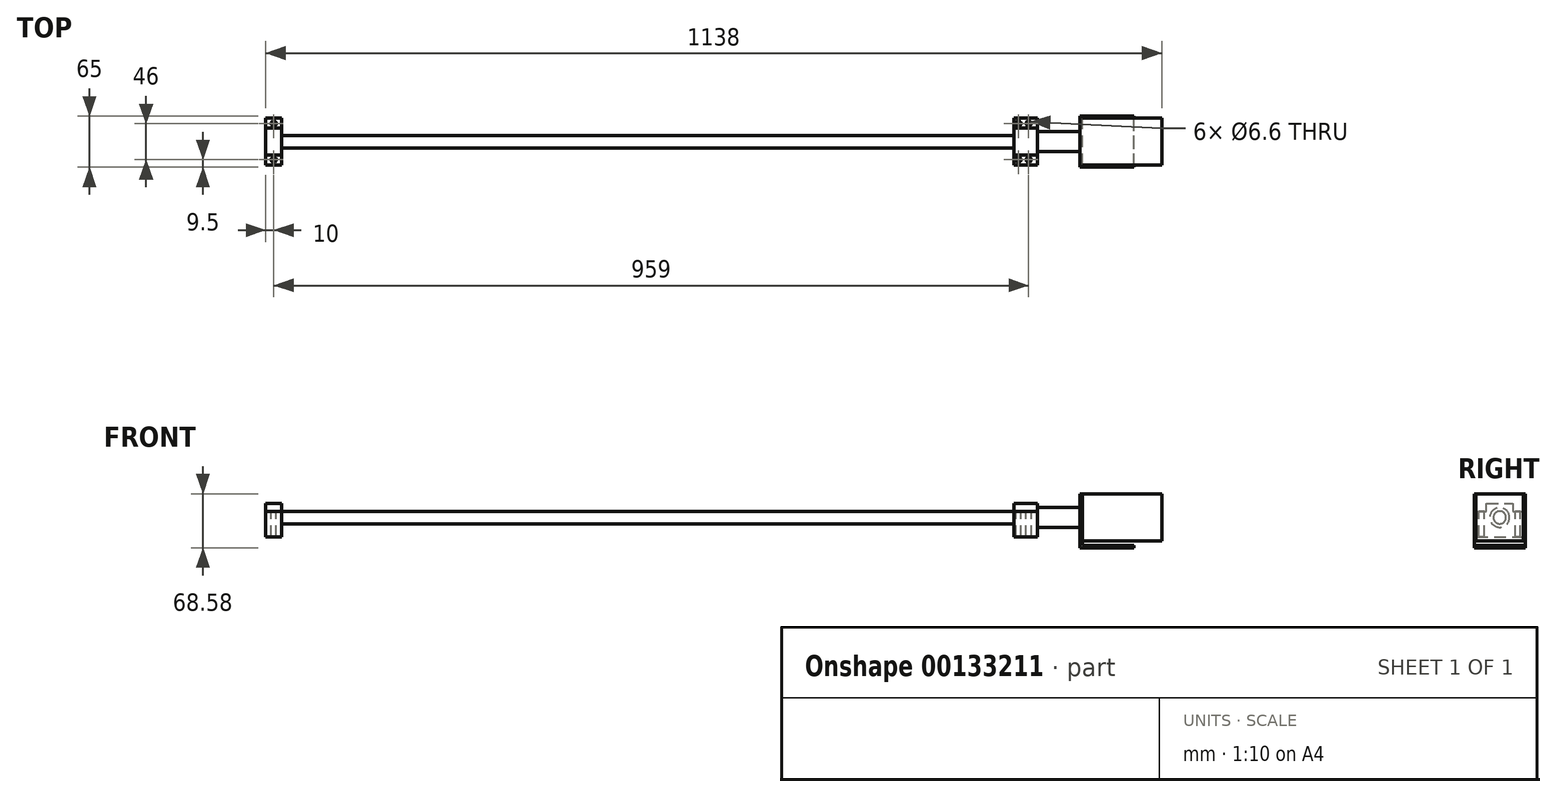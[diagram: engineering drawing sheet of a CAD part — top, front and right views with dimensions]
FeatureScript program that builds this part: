
annotation { "Feature Type Name" : "Feature", "Feature Type Description" : "" }
export const myFeature = defineFeature(function(context is Context, id is Id, definition is map)
    precondition{}
    {
        {
            var Q0;
            Q0=qCreatedBy(makeId("Right.planeOp"),FACE);
            var sketch = newSketch(context, id + "F0", { "sketchPlane" : qUnion([Q0])});
            skCircle(sketch, "E0", {"center": v(0, 0) * mm, "radius": 8 * mm});
            skSolve(sketch);
        }
        {
            var Q0;
            Q0=qSketchRegion(id+"F0",true);
            var Q1;
            Q1 = qSketchRegion(id + "F2", true);
            extrude(context, id + "F1", {"entities" : qUnion([Q0, Q1]), "depth" : 980 * mm, "offsetDistance" : 25 * mm});
        }
        {
            var Q0;
            Q0=makeQuery(id+"F1.opExtrude","CAP_FACE",FACE,{"disambiguationData":[OSD([sQuery(id+"F0.wireOp",EDGE,"E0")])],"isStart":false});
            var sketch = newSketch(context, id + "F2", { "sketchPlane" : qUnion([Q0])});
            skLineSegment(sketch, "E1.bottom", {"start": v(17, 7.5) * mm, "end": v(30, 7.5) * mm});
            skLineSegment(sketch, "E1.top", {"start": v(-30, -25) * mm, "end": v(30, -25) * mm});
            skLineSegment(sketch, "E1.left", {"start": v(-30, 7.5) * mm, "end": v(-30, -25) * mm});
            skLineSegment(sketch, "E1.right", {"start": v(30, 7.5) * mm, "end": v(30, -25) * mm});
            skLineSegment(sketch, "E2", {"start": v(-17, 7.5) * mm, "end": v(-17, 18) * mm});
            skLineSegment(sketch, "E3", {"start": v(-17, 18) * mm, "end": v(17, 18) * mm});
            skLineSegment(sketch, "E4", {"start": v(17, 18) * mm, "end": v(17, 7.5) * mm});
            skLineSegment(sketch, "E5", {"start": v(-30, 7.5) * mm, "end": v(-17, 7.5) * mm});
            skSolve(sketch);
        }
        {
            var Q0;
            Q0=qSketchRegion(id+"F2",true);
            extrude(context, id + "F3", {"entities" : qUnion([Q0]), "operationType" : NewBodyOperationType.ADD, "oppositeDirection" : true, "depth" : (30) * mm, "offsetDistance" : 25 * mm});
        }
        {
            var Q0;
            Q0=makeQuery(id+"F1.opExtrude","CAP_FACE",FACE,{"disambiguationData":[OSD([sQuery(id+"F0.wireOp",EDGE,"E0")])],"isStart":true});
            var sketch = newSketch(context, id + "F4", { "sketchPlane" : qUnion([Q0])});
            skLineSegment(sketch, "E6.0", {"start": v(17, 18) * mm, "end": v(-17, 18) * mm});
            skLineSegment(sketch, "E7.0", {"start": v(-17, 18) * mm, "end": v(-17, 7.5) * mm});
            skLineSegment(sketch, "E8.0", {"start": v(-30, 7.5) * mm, "end": v(-30, -25) * mm});
            skLineSegment(sketch, "E9.0", {"start": v(30, -25) * mm, "end": v(-30, -25) * mm});
            skLineSegment(sketch, "E10.0", {"start": v(30, 7.5) * mm, "end": v(30, -25) * mm});
            skLineSegment(sketch, "E11.0", {"start": v(30, 7.5) * mm, "end": v(17, 7.5) * mm});
            skLineSegment(sketch, "E12.0", {"start": v(17, 7.5) * mm, "end": v(17, 18) * mm});
            skLineSegment(sketch, "E13", {"start": v(-30, 7.5) * mm, "end": v(-17, 7.5) * mm});
            skSolve(sketch);
        }
        {
            var Q0;
            Q0=qSketchRegion(id+"F4",true);
            extrude(context, id + "F5", {"entities" : qUnion([Q0]), "operationType" : NewBodyOperationType.ADD, "oppositeDirection" : true, "depth" : (20) * mm, "offsetDistance" : 25 * mm});
        }
        {
            var Q0;
            Q0=makeQuery(id+"F3.boolean.opBoolean","MERGE",FACE,{"derivedFrom":[makeQuery(id+"F1.opExtrude","CAP_FACE",FACE,{"disambiguationData":[OSD([sQuery(id+"F0.wireOp",EDGE,"E0")])],"isStart":false}),makeQuery(id+"F3.opExtrude","CAP_FACE",FACE,{"disambiguationData":[OSD([sQuery(id+"F2.wireOp",EDGE,"E1.bottom"),sQuery(id+"F2.wireOp",EDGE,"E1.top"),sQuery(id+"F2.wireOp",EDGE,"E1.left"),sQuery(id+"F2.wireOp",EDGE,"E1.right"),sQuery(id+"F2.wireOp",EDGE,"E2"),sQuery(id+"F2.wireOp",EDGE,"E3"),sQuery(id+"F2.wireOp",EDGE,"E4"),sQuery(id+"F2.wireOp",EDGE,"E5")])],"isStart":true})]});
            var sketch = newSketch(context, id + "F6", { "sketchPlane" : qUnion([Q0])});
            skCircle(sketch, "E14", {"center": v(0, 0) * mm, "radius": 12.5 * mm});
            skSolve(sketch);
        }
        {
            var Q0;
            Q0=qSketchRegion(id+"F6",true);
            extrude(context, id + "F7", {"entities" : qUnion([Q0]), "operationType" : NewBodyOperationType.ADD, "depth" : (57) * mm, "offsetDistance" : 25 * mm});
        }
        {
            var Q0;
            Q0=makeQuery(id+"F3.opExtrude","SWEPT_FACE",FACE,{"disambiguationData":[OSD([sQuery(id+"F2.wireOp",EDGE,"E3")])]});
            var sketch = newSketch(context, id + "F8", { "sketchPlane" : qUnion([Q0])});
            skCircle(sketch, "E15", {"center": v(956, 23) * mm, "radius": 3.3 * mm});
            skCircle(sketch, "E16", {"center": v(969, 23) * mm, "radius": 3.3 * mm});
            skCircle(sketch, "E17", {"center": v(956, -23) * mm, "radius": 3.3 * mm});
            skCircle(sketch, "E18", {"center": v(969, -23) * mm, "radius": 3.3 * mm});
            skCircle(sketch, "E19", {"center": v(10, 23) * mm, "radius": 3.3 * mm});
            skCircle(sketch, "E20", {"center": v(10, -23) * mm, "radius": 3.3 * mm});
            skSolve(sketch);
        }
        {
            var Q0;
            Q0=qSketchRegion(id+"F8",true);
            extrude(context, id + "F9", {"entities" : qUnion([Q0]), "operationType" : NewBodyOperationType.REMOVE, "endBound" : BoundingType.THROUGH_ALL, "oppositeDirection" : true, "depth" : 25 * mm, "offsetDistance" : 25 * mm});
        }
        {
            var Q0;
            Q0=makeQuery(id+"F7.opExtrude","CAP_FACE",FACE,{"disambiguationData":[OSD([sQuery(id+"F6.wireOp",EDGE,"E14")])],"isStart":false});
            var sketch = newSketch(context, id + "F10", { "sketchPlane" : qUnion([Q0])});
            skLineSegment(sketch, "E21.bottom", {"start": v(-30, 30) * mm, "end": v(30, 30) * mm});
            skLineSegment(sketch, "E21.top", {"start": v(-30, -30) * mm, "end": v(30, -30) * mm});
            skLineSegment(sketch, "E21.left", {"start": v(-30, 30) * mm, "end": v(-30, -30) * mm});
            skLineSegment(sketch, "E21.right", {"start": v(30, 30) * mm, "end": v(30, -30) * mm});
            skSolve(sketch);
        }
        {
            var Q0;
            Q0=qSketchRegion(id+"F10",true);
            extrude(context, id + "F11", {"entities" : qUnion([Q0]), "operationType" : NewBodyOperationType.ADD, "depth" : (101) * mm, "offsetDistance" : 25 * mm});
        }
        {
            var Q0;
            Q0=qCreatedBy(makeId("Front.planeOp"),FACE);
            var sketch = newSketch(context, id + "F12", { "sketchPlane" : qUnion([Q0])});
            skLineSegment(sketch, "E22.bottom", {"start": v(1034, 30) * mm, "end": v(1037, 30) * mm});
            skLineSegment(sketch, "E22.left", {"start": v(1034, 30) * mm, "end": v(1034, -38.58) * mm});
            skLineSegment(sketch, "E22.right", {"start": v(1037, 30) * mm, "end": v(1037, -35.58) * mm});
            skLineSegment(sketch, "E23.bottom", {"start": v(1034, -38.58) * mm, "end": v(1102.58, -38.58) * mm});
            skLineSegment(sketch, "E23.top", {"start": v(1037, -35.58) * mm, "end": v(1102.58, -35.58) * mm});
            skLineSegment(sketch, "E23.right", {"start": v(1102.58, -38.58) * mm, "end": v(1102.58, -35.58) * mm});
            skSolve(sketch);
        }
        {
            var Q0;
            Q0=qSketchRegion(id+"F12",true);
            extrude(context, id + "F13", {"entities" : qUnion([Q0]), "operationType" : NewBodyOperationType.ADD, "depth" : (65) * mm, "offsetDistance" : 25 * mm, "symmetric" : true});
        }
    });
